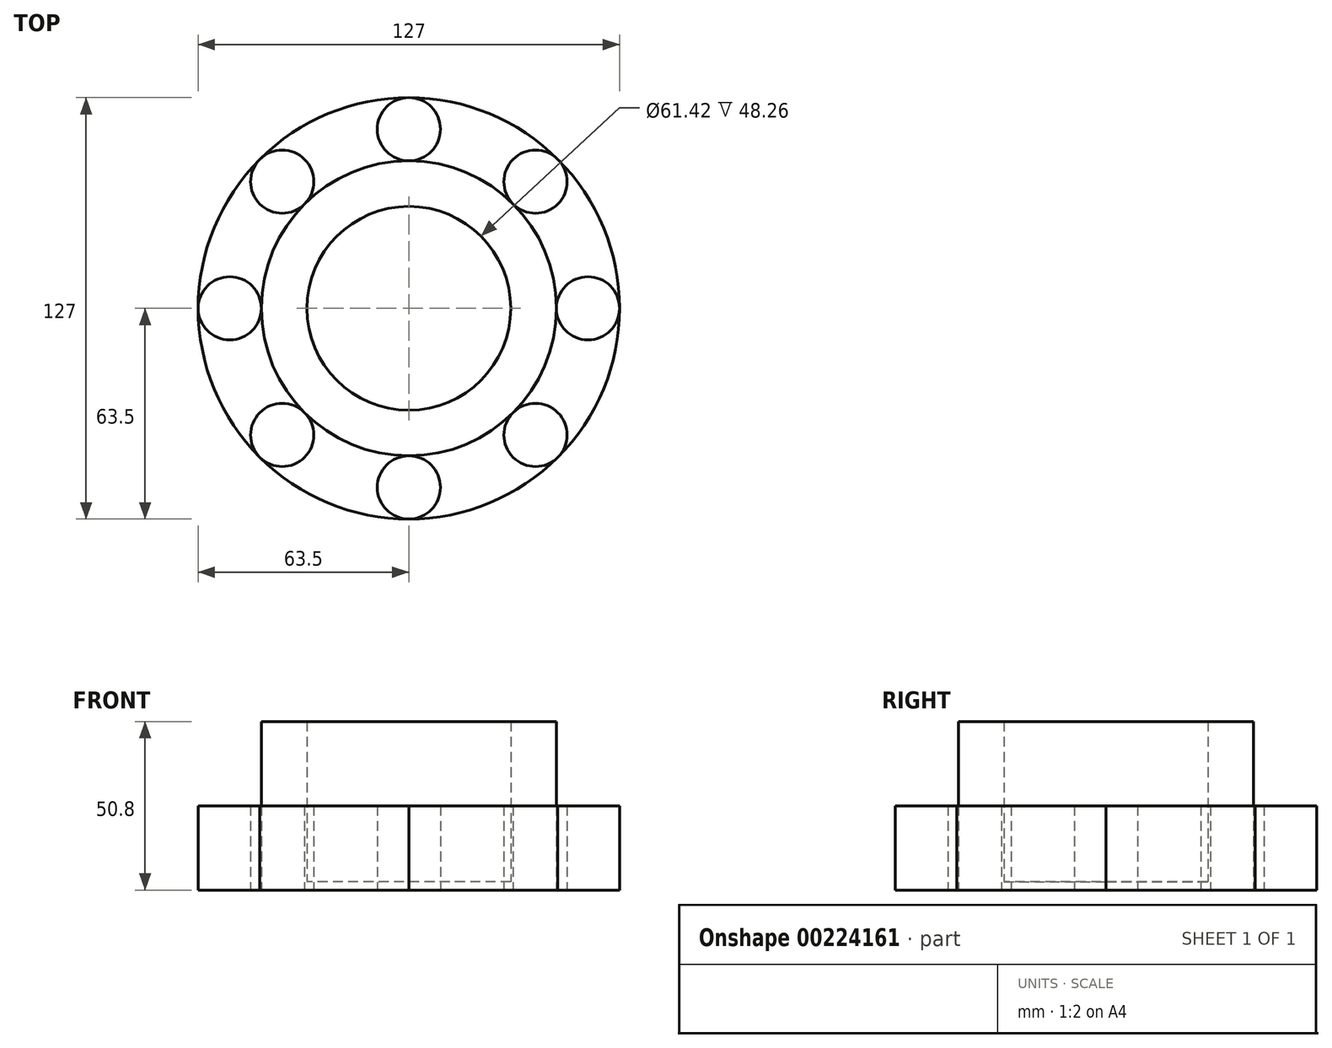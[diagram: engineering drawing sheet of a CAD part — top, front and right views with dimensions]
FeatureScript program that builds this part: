
annotation { "Feature Type Name" : "Feature", "Feature Type Description" : "" }
export const myFeature = defineFeature(function(context is Context, id is Id, definition is map)
    precondition{}
    {
        {
            var Q0;
            Q0=qCreatedBy(makeId("Top.planeOp"),FACE);
            var sketch = newSketch(context, id + "F0", { "sketchPlane" : qUnion([Q0])});
            skCircle(sketch, "E0", {"center": v(0, 0) * mm, "radius": 44.45 * mm});
            skCircle(sketch, "E1", {"center": v(0, 0) * mm, "radius": 63.5 * mm});
            skCircle(sketch, "E2", {"center": v(38.17, 38.17) * mm, "radius": 9.52 * mm});
            skCircle(sketch, "E3.1.0", {"center": v(0, 53.97) * mm, "radius": 9.52 * mm});
            skCircle(sketch, "E3.2.0", {"center": v(-38.17, 38.17) * mm, "radius": 9.52 * mm});
            skCircle(sketch, "E4.1.3.0", {"center": v(-53.98, 0) * mm, "radius": 9.52 * mm});
            skCircle(sketch, "E4.1.4.0", {"center": v(-38.17, -38.17) * mm, "radius": 9.52 * mm});
            skCircle(sketch, "E4.1.5.0", {"center": v(0, -53.97) * mm, "radius": 9.52 * mm});
            skCircle(sketch, "E4.1.6.0", {"center": v(38.17, -38.17) * mm, "radius": 9.52 * mm});
            skCircle(sketch, "E4.1.7.0", {"center": v(53.97, 0) * mm, "radius": 9.52 * mm});
            skCircle(sketch, "E5", {"center": v(0, 0) * mm, "radius": 30.71 * mm});
            skLineSegment(sketch, "E6", {"start": v(0, 44.45) * mm, "end": v(0, -44.45) * mm});
            skLineSegment(sketch, "E7", {"start": v(0, -44.45) * mm, "end": v(0, 0) * mm});
            skLineSegment(sketch, "E8", {"start": v(-44.45, 0) * mm, "end": v(44.45, 0) * mm});
            skCircle(sketch, "E9", {"center": v(0, 0) * mm, "radius": 83.82 * mm});
            skLineSegment(sketch, "E10", {"start": v(-47.34, -42.33) * mm, "end": v(-62.49, -55.87) * mm});
            skLineSegment(sketch, "E11", {"start": v(0, 0) * mm, "end": v(-83.82, 0) * mm});
            skLineSegment(sketch, "E12", {"start": v(-83.82, 0) * mm, "end": v(0, 0) * mm});
            skLineSegment(sketch, "E13", {"start": v(0, 0) * mm, "end": v(0, -83.82) * mm});
            skLineSegment(sketch, "E14", {"start": v(0, -83.82) * mm, "end": v(0, 0) * mm});
            skLineSegment(sketch, "E15.bottom", {"start": v(0, 0) * mm, "end": v(-83.27, 0) * mm});
            skLineSegment(sketch, "E15.left", {"start": v(0, 0) * mm, "end": v(0, -84.16) * mm});
            skLineSegment(sketch, "E16", {"start": v(0, 0) * mm, "end": v(-83.72, -83.72) * mm});
            skLineSegment(sketch, "E17", {"start": v(0, 0) * mm, "end": v(0, 53.97) * mm});
            skSolve(sketch);
        }
        {
            var Q0;
            {var subQ0=sQuery(id+"F0.wireOp",EDGE,"E4.1.7.0");var subQ1=sQuery(id+"F0.wireOp",EDGE,"E0");var subQ2=makeQuery(id+"F0.imprint","INTERSECT",VERTEX,{"derivedFrom":[subQ1,subQ0]});Q0=makeQuery(id+"F0.imprint","IMPRINT",FACE,{"disambiguationData":[TD([[makeQuery(id+"F0.imprint","IMPRINT",EDGE,{"disambiguationData":[TD([[subQ2,1.0]])],"derivedFrom":subQ1}),-1.0]])]});}
            var Q1;
            {var subQ0=sQuery(id+"F0.wireOp",EDGE,"E4.1.5.0");var subQ1=sQuery(id+"F0.wireOp",EDGE,"E0");var subQ2=makeQuery(id+"F0.imprint","INTERSECT",VERTEX,{"derivedFrom":[subQ1,subQ0]});Q1=makeQuery(id+"F0.imprint","IMPRINT",FACE,{"disambiguationData":[TD([[makeQuery(id+"F0.imprint","IMPRINT",EDGE,{"disambiguationData":[TD([[subQ2,-1.0]])],"derivedFrom":subQ1}),-1.0]])]});}
            var Q2;
            {var subQ0=sQuery(id+"F0.wireOp",EDGE,"E4.1.4.0");var subQ1=sQuery(id+"F0.wireOp",EDGE,"E0");var subQ2=makeQuery(id+"F0.imprint","INTERSECT",VERTEX,{"derivedFrom":[subQ1,subQ0]});Q2=makeQuery(id+"F0.imprint","IMPRINT",FACE,{"disambiguationData":[TD([[makeQuery(id+"F0.imprint","IMPRINT",EDGE,{"disambiguationData":[TD([[subQ2,-1.0]])],"derivedFrom":subQ1}),-1.0]])]});}
            var Q3;
            {var subQ0=sQuery(id+"F0.wireOp",EDGE,"E4.1.3.0");var subQ1=sQuery(id+"F0.wireOp",EDGE,"E0");var subQ2=makeQuery(id+"F0.imprint","INTERSECT",VERTEX,{"derivedFrom":[subQ1,subQ0]});Q3=makeQuery(id+"F0.imprint","IMPRINT",FACE,{"disambiguationData":[TD([[makeQuery(id+"F0.imprint","IMPRINT",EDGE,{"disambiguationData":[TD([[subQ2,-1.0]])],"derivedFrom":subQ1}),-1.0]])]});}
            var Q4;
            {var subQ0=sQuery(id+"F0.wireOp",EDGE,"E3.2.0");var subQ1=sQuery(id+"F0.wireOp",EDGE,"E0");var subQ2=makeQuery(id+"F0.imprint","INTERSECT",VERTEX,{"derivedFrom":[subQ1,subQ0]});Q4=makeQuery(id+"F0.imprint","IMPRINT",FACE,{"disambiguationData":[TD([[makeQuery(id+"F0.imprint","IMPRINT",EDGE,{"disambiguationData":[TD([[subQ2,-1.0]])],"derivedFrom":subQ1}),-1.0]])]});}
            var Q5;
            {var subQ0=sQuery(id+"F0.wireOp",EDGE,"E2");var subQ1=sQuery(id+"F0.wireOp",EDGE,"E0");var subQ2=makeQuery(id+"F0.imprint","INTERSECT",VERTEX,{"derivedFrom":[subQ1,subQ0]});Q5=makeQuery(id+"F0.imprint","IMPRINT",FACE,{"disambiguationData":[TD([[makeQuery(id+"F0.imprint","IMPRINT",EDGE,{"disambiguationData":[TD([[subQ2,1.0]])],"derivedFrom":subQ1}),-1.0]])]});}
            var Q6;
            {var subQ0=sQuery(id+"F0.wireOp",EDGE,"E2");var subQ1=sQuery(id+"F0.wireOp",EDGE,"E0");var subQ2=makeQuery(id+"F0.imprint","INTERSECT",VERTEX,{"derivedFrom":[subQ1,subQ0]});Q6=makeQuery(id+"F0.imprint","IMPRINT",FACE,{"disambiguationData":[TD([[makeQuery(id+"F0.imprint","IMPRINT",EDGE,{"disambiguationData":[TD([[subQ2,-1.0]])],"derivedFrom":subQ1}),-1.0]])]});}
            var Q7;
            {var subQ0=sQuery(id+"F0.wireOp",EDGE,"E3.1.0");var subQ1=sQuery(id+"F0.wireOp",EDGE,"E0");var subQ2=makeQuery(id+"F0.imprint","INTERSECT",VERTEX,{"derivedFrom":[subQ1,subQ0]});Q7=makeQuery(id+"F0.imprint","IMPRINT",FACE,{"disambiguationData":[TD([[makeQuery(id+"F0.imprint","IMPRINT",EDGE,{"disambiguationData":[TD([[subQ2,-1.0]])],"derivedFrom":subQ1}),-1.0]])]});}
            var Q8;
            Q8=sQuery(id+"F0.wireOp",EDGE,"E5");
            extrude(context, id + "F1", {"entities" : qUnion([Q0, Q1, Q2, Q3, Q4, Q5, Q6, Q7]), "surfaceEntities" : qUnion([Q8]), "depth" : 25.4 * mm});
        }
        {
            var Q0;
            {var subQ3=sQuery(id+"F0.wireOp",EDGE,"E8");var subQ5=sQuery(id+"F0.wireOp",EDGE,"E0");var subQ8=makeQuery(id+"F0.imprint","INTERSECT",VERTEX,{"disambiguationData":[OD(1.0)],"derivedFrom":[subQ5,subQ3]});Q0=makeQuery(id+"F0.imprint","IMPRINT",FACE,{"disambiguationData":[TD([[makeQuery(id+"F0.imprint","IMPRINT",EDGE,{"disambiguationData":[TD([[subQ8,-1.0]])],"derivedFrom":subQ5}),1.0]])]});}
            var Q1;
            {var subQ0=sQuery(id+"F0.wireOp",EDGE,"E6");var subQ5=sQuery(id+"F0.wireOp",EDGE,"E0");var subQ9=makeQuery(id+"F0.imprint","INTERSECT",VERTEX,{"derivedFrom":[subQ5,subQ0]});Q1=makeQuery(id+"F0.imprint","IMPRINT",FACE,{"disambiguationData":[TD([[makeQuery(id+"F0.imprint","IMPRINT",EDGE,{"disambiguationData":[TD([[subQ9,-1.0]])],"derivedFrom":subQ5}),1.0]])]});}
            var Q2;
            {var subQ0=sQuery(id+"F0.wireOp",EDGE,"E8");var subQ5=sQuery(id+"F0.wireOp",EDGE,"E0");var subQ6=makeQuery(id+"F0.imprint","INTERSECT",VERTEX,{"disambiguationData":[OD(0.0)],"derivedFrom":[subQ5,subQ0]});Q2=makeQuery(id+"F0.imprint","IMPRINT",FACE,{"disambiguationData":[TD([[makeQuery(id+"F0.imprint","IMPRINT",EDGE,{"disambiguationData":[TD([[subQ6,-1.0]])],"derivedFrom":subQ5}),1.0]])]});}
            var Q3;
            {var subQ3=sQuery(id+"F0.wireOp",EDGE,"E7");var subQ5=sQuery(id+"F0.wireOp",EDGE,"E0");var subQ9=makeQuery(id+"F0.imprint","INTERSECT",VERTEX,{"derivedFrom":[subQ5,subQ3]});Q3=makeQuery(id+"F0.imprint","IMPRINT",FACE,{"disambiguationData":[TD([[makeQuery(id+"F0.imprint","IMPRINT",EDGE,{"disambiguationData":[TD([[subQ9,-1.0]])],"derivedFrom":subQ5}),1.0]])]});}
            var Q4;
            {var subQ0=sQuery(id+"F0.wireOp",EDGE,"E15.bottom");var subQ5=sQuery(id+"F0.wireOp",EDGE,"E5");var subQ6=makeQuery(id+"F0.imprint","INTERSECT",VERTEX,{"derivedFrom":[subQ5,subQ0]});Q4=makeQuery(id+"F0.imprint","IMPRINT",FACE,{"disambiguationData":[TD([[makeQuery(id+"F0.imprint","IMPRINT",EDGE,{"disambiguationData":[TD([[subQ6,-1.0]])],"derivedFrom":subQ5}),-1.0]])]});}
            var Q5;
            {var subQ0=sQuery(id+"F0.wireOp",EDGE,"E16");var subQ5=sQuery(id+"F0.wireOp",EDGE,"E5");var subQ6=makeQuery(id+"F0.imprint","INTERSECT",VERTEX,{"derivedFrom":[subQ5,subQ0]});Q5=makeQuery(id+"F0.imprint","IMPRINT",FACE,{"disambiguationData":[TD([[makeQuery(id+"F0.imprint","IMPRINT",EDGE,{"disambiguationData":[TD([[subQ6,-1.0]])],"derivedFrom":subQ5}),-1.0]])]});}
            extrude(context, id + "F2", {"entities" : qUnion([Q0, Q1, Q2, Q3, Q4, Q5]), "depth" : 50.8 * mm});
        }
        {
            var Q0;
            {var subQ0=sQuery(id+"F0.wireOp",EDGE,"E17");var subQ1=sQuery(id+"F0.wireOp",EDGE,"E5");var subQ2=makeQuery(id+"F0.imprint","INTERSECT",VERTEX,{"derivedFrom":[subQ1,subQ0]});Q0=makeQuery(id+"F0.imprint","IMPRINT",FACE,{"disambiguationData":[TD([[makeQuery(id+"F0.imprint","IMPRINT",EDGE,{"disambiguationData":[TD([[subQ2,1.0]])],"derivedFrom":subQ1}),1.0]])]});}
            var Q1;
            {var subQ0=sQuery(id+"F0.wireOp",EDGE,"E8");var subQ1=sQuery(id+"F0.wireOp",EDGE,"E5");var subQ2=makeQuery(id+"F0.imprint","INTERSECT",VERTEX,{"derivedFrom":[subQ1,subQ0]});Q1=makeQuery(id+"F0.imprint","IMPRINT",FACE,{"disambiguationData":[TD([[makeQuery(id+"F0.imprint","IMPRINT",EDGE,{"disambiguationData":[TD([[subQ2,1.0]])],"derivedFrom":subQ1}),1.0]])]});}
            var Q2;
            {var subQ0=sQuery(id+"F0.wireOp",EDGE,"E16");var subQ1=sQuery(id+"F0.wireOp",EDGE,"E5");var subQ2=makeQuery(id+"F0.imprint","INTERSECT",VERTEX,{"derivedFrom":[subQ1,subQ0]});Q2=makeQuery(id+"F0.imprint","IMPRINT",FACE,{"disambiguationData":[TD([[makeQuery(id+"F0.imprint","IMPRINT",EDGE,{"disambiguationData":[TD([[subQ2,-1.0]])],"derivedFrom":subQ1}),1.0]])]});}
            var Q3;
            {var subQ0=sQuery(id+"F0.wireOp",EDGE,"E15.bottom");var subQ1=sQuery(id+"F0.wireOp",EDGE,"E5");var subQ2=makeQuery(id+"F0.imprint","INTERSECT",VERTEX,{"derivedFrom":[subQ1,subQ0]});Q3=makeQuery(id+"F0.imprint","IMPRINT",FACE,{"disambiguationData":[TD([[makeQuery(id+"F0.imprint","IMPRINT",EDGE,{"disambiguationData":[TD([[subQ2,-1.0]])],"derivedFrom":subQ1}),1.0]])]});}
            var Q4;
            {var subQ0=sQuery(id+"F0.wireOp",EDGE,"E17");var subQ1=sQuery(id+"F0.wireOp",EDGE,"E5");var subQ2=makeQuery(id+"F0.imprint","INTERSECT",VERTEX,{"derivedFrom":[subQ1,subQ0]});Q4=makeQuery(id+"F0.imprint","IMPRINT",FACE,{"disambiguationData":[TD([[makeQuery(id+"F0.imprint","IMPRINT",EDGE,{"disambiguationData":[TD([[subQ2,-1.0]])],"derivedFrom":subQ1}),1.0]])]});}
            extrude(context, id + "F3", {"entities" : qUnion([Q0, Q1, Q2, Q3, Q4]), "operationType" : NewBodyOperationType.ADD, "depth" : 2.54 * mm});
        }
    });
